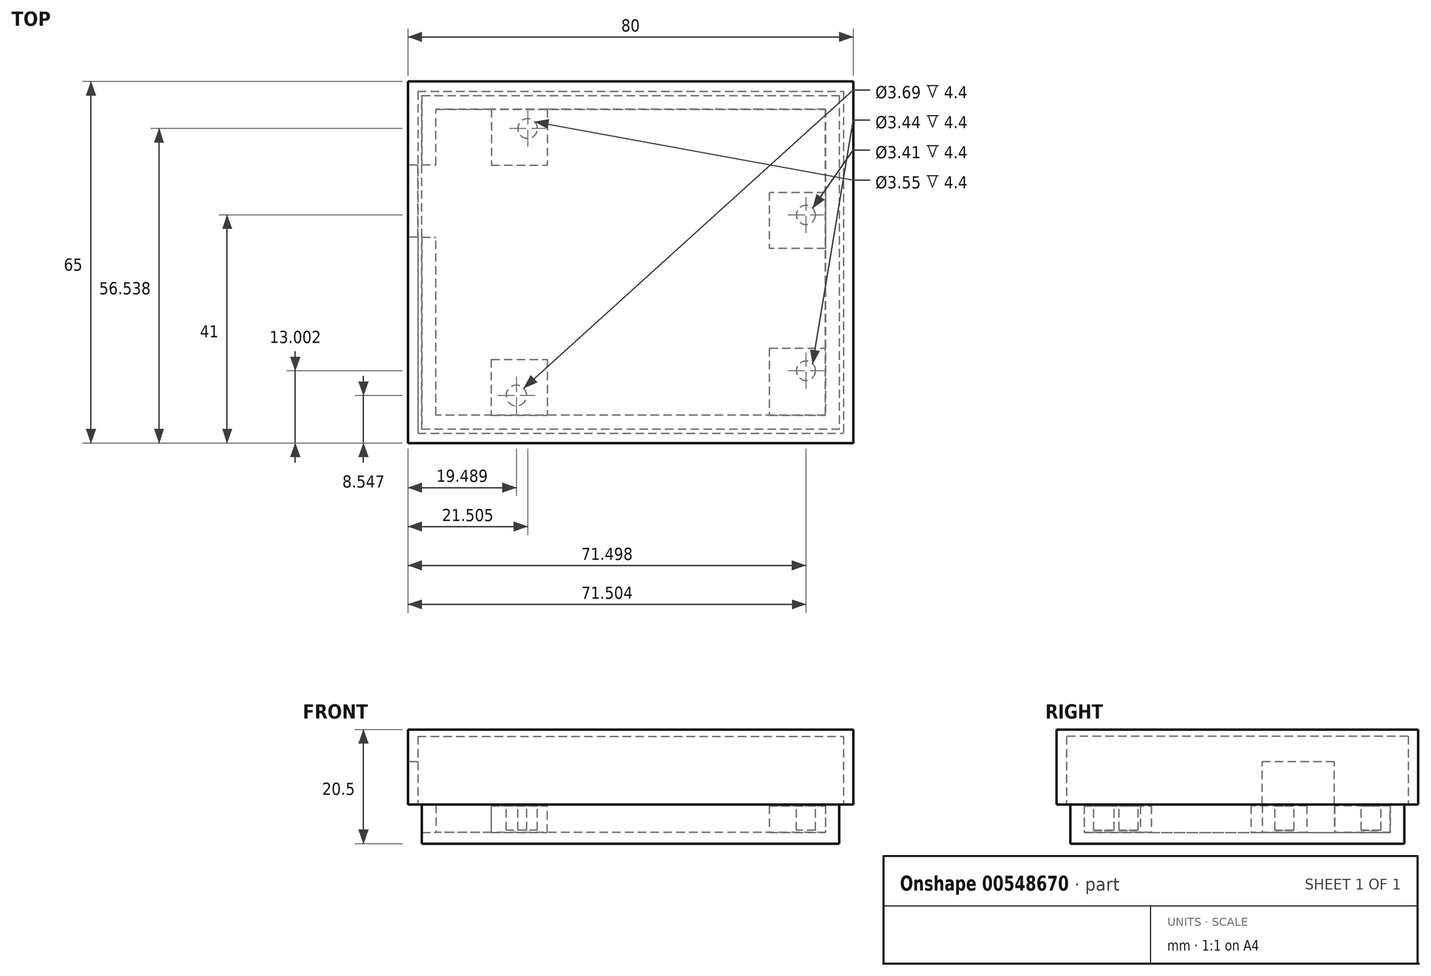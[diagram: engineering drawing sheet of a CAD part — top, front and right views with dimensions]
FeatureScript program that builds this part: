
annotation { "Feature Type Name" : "Feature", "Feature Type Description" : "" }
export const myFeature = defineFeature(function(context is Context, id is Id, definition is map)
    precondition{}
    {
        {
            var Q0;
            Q0=qCreatedBy(makeId("Top.planeOp"),FACE);
            var sketch = newSketch(context, id + "F0", { "sketchPlane" : qUnion([Q0])});
            skLineSegment(sketch, "E0.rect.bottom", {"start": v(37.5, -30) * mm, "end": v(-37.5, -30) * mm});
            skLineSegment(sketch, "E0.rect.top", {"start": v(37.5, 30) * mm, "end": v(-37.5, 30) * mm});
            skLineSegment(sketch, "E0.rect.left", {"start": v(37.5, -30) * mm, "end": v(37.5, 30) * mm});
            skLineSegment(sketch, "E0.rect.right", {"start": v(-37.5, -30) * mm, "end": v(-37.5, 30) * mm});
            skPoint(sketch, "E0.rect.middle", {"position": v(0, 0) * mm});
            skSolve(sketch);
        }
        {
            var Q0;
            Q0=qSketchRegion(id+"F0",true);
            extrude(context, id + "F1", {"entities" : qUnion([Q0]), "depth" : 2 * mm});
        }
        {
            var Q0;
            Q0=makeQuery(id+"F1.opExtrude","CAP_FACE",FACE,{"disambiguationData":[OSD([sQuery(id+"F0.wireOp",EDGE,"E0.rect.bottom"),sQuery(id+"F0.wireOp",EDGE,"E0.rect.top"),sQuery(id+"F0.wireOp",EDGE,"E0.rect.left"),sQuery(id+"F0.wireOp",EDGE,"E0.rect.right")])],"isStart":false});
            var sketch = newSketch(context, id + "F2", { "sketchPlane" : qUnion([Q0])});
            skLineSegment(sketch, "E1.rect.bottom", {"start": v(35, -27.5) * mm, "end": v(-35, -27.5) * mm});
            skLineSegment(sketch, "E1.rect.top", {"start": v(35, 27.5) * mm, "end": v(-35, 27.5) * mm});
            skLineSegment(sketch, "E1.rect.left", {"start": v(35, -27.5) * mm, "end": v(35, 27.5) * mm});
            skLineSegment(sketch, "E1.rect.right", {"start": v(-35, -27.5) * mm, "end": v(-35, 27.5) * mm});
            skPoint(sketch, "E1.rect.middle", {"position": v(0, 0) * mm});
            skLineSegment(sketch, "E2.rect.bottom", {"start": v(37.5, -30) * mm, "end": v(-37.5, -30) * mm});
            skLineSegment(sketch, "E2.rect.top", {"start": v(37.5, 30) * mm, "end": v(-37.5, 30) * mm});
            skLineSegment(sketch, "E2.rect.left", {"start": v(37.5, -30) * mm, "end": v(37.5, 30) * mm});
            skLineSegment(sketch, "E2.rect.right", {"start": v(-37.5, -30) * mm, "end": v(-37.5, 30) * mm});
            skSolve(sketch);
        }
        {
            var Q0;
            Q0=qSketchRegion(id+"F2",true);
            extrude(context, id + "F3", {"entities" : qUnion([Q0]), "operationType" : NewBodyOperationType.ADD, "depth" : 15 * mm});
        }
        {
            var Q0;
            Q0=makeQuery(id+"F1.opExtrude","CAP_FACE",FACE,{"disambiguationData":[OSD([sQuery(id+"F0.wireOp",EDGE,"E0.rect.bottom"),sQuery(id+"F0.wireOp",EDGE,"E0.rect.top"),sQuery(id+"F0.wireOp",EDGE,"E0.rect.left"),sQuery(id+"F0.wireOp",EDGE,"E0.rect.right")])],"isStart":false});
            var sketch = newSketch(context, id + "F4", { "sketchPlane" : qUnion([Q0])});
            skLineSegment(sketch, "E3.bottom", {"start": v(-25, 27.5) * mm, "end": v(-15, 27.5) * mm});
            skLineSegment(sketch, "E3.top", {"start": v(-25, 17.5) * mm, "end": v(-15, 17.5) * mm});
            skLineSegment(sketch, "E3.left", {"start": v(-25, 27.5) * mm, "end": v(-25, 17.5) * mm});
            skLineSegment(sketch, "E3.right", {"start": v(-15, 27.5) * mm, "end": v(-15, 17.5) * mm});
            skLineSegment(sketch, "E4.bottom", {"start": v(-25, -27.5) * mm, "end": v(-15, -27.5) * mm});
            skLineSegment(sketch, "E4.top", {"start": v(-25, -17.5) * mm, "end": v(-15, -17.5) * mm});
            skLineSegment(sketch, "E4.left", {"start": v(-25, -27.5) * mm, "end": v(-25, -17.5) * mm});
            skLineSegment(sketch, "E4.right", {"start": v(-15, -27.5) * mm, "end": v(-15, -17.5) * mm});
            skLineSegment(sketch, "E5.bottom", {"start": v(35, -27.5) * mm, "end": v(25, -27.5) * mm});
            skLineSegment(sketch, "E5.top", {"start": v(35, -15.5) * mm, "end": v(25, -15.5) * mm});
            skLineSegment(sketch, "E5.left", {"start": v(35, -27.5) * mm, "end": v(35, -15.5) * mm});
            skLineSegment(sketch, "E5.right", {"start": v(25, -27.5) * mm, "end": v(25, -15.5) * mm});
            skLineSegment(sketch, "E6.bottom", {"start": v(35, 12.5) * mm, "end": v(25, 12.5) * mm});
            skLineSegment(sketch, "E6.top", {"start": v(35, 2.5) * mm, "end": v(25, 2.5) * mm});
            skLineSegment(sketch, "E6.left", {"start": v(35, 12.5) * mm, "end": v(35, 2.5) * mm});
            skLineSegment(sketch, "E6.right", {"start": v(25, 12.5) * mm, "end": v(25, 2.5) * mm});
            skSolve(sketch);
        }
        {
            var Q0;
            Q0=makeQuery(id+"F4.imprint","IMPRINT",FACE,{"disambiguationData":[TD([[makeQuery(id+"F4.imprint","IMPRINT",EDGE,{"derivedFrom":sQuery(id+"F4.wireOp",EDGE,"E3.top")}),-1.0]])]});
            cPlane(context, id + "F5", {"entities" : qUnion([Q0]), "cplaneType" : CPlaneType.OFFSET, "offset" : 5 * mm, "width" : 150 * mm, "height" : 150 * mm});
        }
        {
            var Q0;
            Q0=makeQuery(id+"F3.opExtrude","SWEPT_FACE",FACE,{"disambiguationData":[OSD([sQuery(id+"F2.wireOp",EDGE,"E1.rect.right")])]});
            var sketch = newSketch(context, id + "F6", { "sketchPlane" : qUnion([Q0])});
            skLineSegment(sketch, "E7.bottom", {"start": v(4.5, 17) * mm, "end": v(17.5, 17) * mm});
            skLineSegment(sketch, "E7.top", {"start": v(4.5, 2) * mm, "end": v(17.5, 2) * mm});
            skLineSegment(sketch, "E7.left", {"start": v(4.5, 17) * mm, "end": v(4.5, 2) * mm});
            skLineSegment(sketch, "E7.right", {"start": v(17.5, 17) * mm, "end": v(17.5, 2) * mm});
            skSolve(sketch);
        }
        {
            var Q0;
            Q0=qSketchRegion(id+"F6",true);
            extrude(context, id + "F7", {"entities" : qUnion([Q0]), "operationType" : NewBodyOperationType.REMOVE, "endBound" : BoundingType.UP_TO_NEXT, "oppositeDirection" : true, "depth" : 25 * mm});
        }
        {
            var Q0;
            Q0=qCreatedBy(id+"F5.planeOp",FACE);
            var sketch = newSketch(context, id + "F8", { "sketchPlane" : qUnion([Q0])});
            skLineSegment(sketch, "E8.bottom", {"start": v(-40, -32.5) * mm, "end": v(40, -32.5) * mm});
            skLineSegment(sketch, "E8.top", {"start": v(-40, 32.5) * mm, "end": v(40, 32.5) * mm});
            skLineSegment(sketch, "E8.left", {"start": v(-40, -32.5) * mm, "end": v(-40, 32.5) * mm});
            skLineSegment(sketch, "E8.right", {"start": v(40, -32.5) * mm, "end": v(40, 32.5) * mm});
            skPoint(sketch, "E8.middle", {"position": v(0, 0) * mm});
            skSolve(sketch);
        }
        {
            var Q0;
            Q0 = qSketchRegion(id + "F8", true);
            extrude(context, id + "F9", {"entities" : qUnion([Q0]), "depth" : 13.5 * mm, "offsetDistance" : 25 * mm});
        }
        {
            var Q0;
            {var subQ27=sQuery(id+"F8.wireOp",EDGE,"E8.top");var subQ36=sQuery(id+"F8.wireOp",EDGE,"E8.bottom");var subQ37=sQuery(id+"F8.wireOp",EDGE,"E8.left");var subQ38=sQuery(id+"F8.wireOp",EDGE,"E8.right");Q0=makeQuery(id+"F9.boolean.opBoolean","SPLIT",FACE,{"disambiguationData":[TD([makeQuery(id+"F1.opExtrude","SWEPT_FACE",FACE,{"disambiguationData":[OSD([sQuery(id+"F0.wireOp",EDGE,"E0.rect.bottom")])]})])],"derivedFrom":makeQuery(id+"F9.opExtrude","CAP_FACE",FACE,{"disambiguationData":[OSD([subQ36,subQ27,subQ37,subQ38])],"isStart":true})});}
            var sketch = newSketch(context, id + "F10", { "sketchPlane" : qUnion([Q0])});
            skLineSegment(sketch, "E9.bottom", {"start": v(-38.22, -30.72) * mm, "end": v(38.22, -30.72) * mm});
            skLineSegment(sketch, "E9.top", {"start": v(-38.22, 30.72) * mm, "end": v(38.22, 30.72) * mm});
            skLineSegment(sketch, "E9.left", {"start": v(-38.22, -30.72) * mm, "end": v(-38.22, 30.72) * mm});
            skLineSegment(sketch, "E9.right", {"start": v(38.22, -30.72) * mm, "end": v(38.22, 30.72) * mm});
            skPoint(sketch, "E9.middle", {"position": v(0, 0) * mm});
            skSolve(sketch);
        }
        {
            var Q0;
            Q0 = qSketchRegion(id + "F10", true);
            extrude(context, id + "F11", {"entities" : qUnion([Q0]), "operationType" : NewBodyOperationType.REMOVE, "oppositeDirection" : true, "depth" : 12.3 * mm, "offsetDistance" : 25 * mm});
        }
        {
            var Q0;
            Q0=makeQuery(id+"F9.opExtrude","SWEPT_FACE",FACE,{"disambiguationData":[OSD([sQuery(id+"F8.wireOp",EDGE,"E8.left")])]});
            var sketch = newSketch(context, id + "F12", { "sketchPlane" : qUnion([Q0])});
            skLineSegment(sketch, "E10.bottom", {"start": v(-17.45, 7) * mm, "end": v(-4.5, 7) * mm});
            skLineSegment(sketch, "E10.top", {"start": v(-17.45, 14.72) * mm, "end": v(-4.5, 14.72) * mm});
            skLineSegment(sketch, "E10.left", {"start": v(-17.45, 7) * mm, "end": v(-17.45, 14.72) * mm});
            skLineSegment(sketch, "E10.right", {"start": v(-4.5, 7) * mm, "end": v(-4.5, 14.72) * mm});
            skSolve(sketch);
        }
        {
            var Q0;
            Q0 = qSketchRegion(id + "F12", true);
            extrude(context, id + "F13", {"entities" : qUnion([Q0]), "operationType" : NewBodyOperationType.REMOVE, "oppositeDirection" : true, "depth" : 25 * mm, "offsetDistance" : 25 * mm});
        }
        {
            var Q0;
            Q0=makeQuery(id+"F4.imprint","IMPRINT",FACE,{"disambiguationData":[TD([[makeQuery(id+"F4.imprint","IMPRINT",EDGE,{"derivedFrom":sQuery(id+"F4.wireOp",EDGE,"E3.top")}),-1.0]])]});
            var sketch = newSketch(context, id + "F14", { "sketchPlane" : qUnion([Q0])});
            skLineSegment(sketch, "E11.bottom", {"start": v(-25.02, 27.52) * mm, "end": v(-14.96, 27.52) * mm});
            skLineSegment(sketch, "E11.top", {"start": v(-25.02, 17.43) * mm, "end": v(-14.96, 17.43) * mm});
            skLineSegment(sketch, "E11.left", {"start": v(-25.02, 27.52) * mm, "end": v(-25.02, 17.43) * mm});
            skLineSegment(sketch, "E11.right", {"start": v(-14.96, 27.52) * mm, "end": v(-14.96, 17.43) * mm});
            skLineSegment(sketch, "E12.bottom", {"start": v(34.99, 12.52) * mm, "end": v(24.9, 12.52) * mm});
            skLineSegment(sketch, "E12.top", {"start": v(34.99, 2.47) * mm, "end": v(24.9, 2.47) * mm});
            skLineSegment(sketch, "E12.left", {"start": v(34.99, 12.52) * mm, "end": v(34.99, 2.47) * mm});
            skLineSegment(sketch, "E12.right", {"start": v(24.9, 12.52) * mm, "end": v(24.9, 2.47) * mm});
            skLineSegment(sketch, "E13.bottom", {"start": v(24.9, -15.45) * mm, "end": v(35.03, -15.45) * mm});
            skLineSegment(sketch, "E13.top", {"start": v(24.9, -27.49) * mm, "end": v(35.03, -27.49) * mm});
            skLineSegment(sketch, "E13.left", {"start": v(24.9, -15.45) * mm, "end": v(24.9, -27.49) * mm});
            skLineSegment(sketch, "E13.right", {"start": v(35.03, -15.45) * mm, "end": v(35.03, -27.49) * mm});
            skLineSegment(sketch, "E14.bottom", {"start": v(-25.04, -17.44) * mm, "end": v(-14.96, -17.44) * mm});
            skLineSegment(sketch, "E14.top", {"start": v(-25.04, -27.49) * mm, "end": v(-14.96, -27.49) * mm});
            skLineSegment(sketch, "E14.left", {"start": v(-25.04, -17.44) * mm, "end": v(-25.04, -27.49) * mm});
            skLineSegment(sketch, "E14.right", {"start": v(-14.96, -17.44) * mm, "end": v(-14.96, -27.49) * mm});
            skSolve(sketch);
        }
        {
            var Q0;
            Q0 = qSketchRegion(id + "F14", true);
            extrude(context, id + "F15", {"entities" : qUnion([Q0]), "operationType" : NewBodyOperationType.ADD, "depth" : 4.8 * mm, "offsetDistance" : 25 * mm});
        }
        {
            var Q0;
            {var subQ6=sQuery(id+"F2.wireOp",EDGE,"E1.rect.top");var subQ9=sQuery(id+"F14.wireOp",EDGE,"E11.left");var subQ10=sQuery(id+"F14.wireOp",EDGE,"E11.top");var subQ11=sQuery(id+"F14.wireOp",EDGE,"E11.right");Q0=makeQuery(id+"F15.boolean.opBoolean","SPLIT",FACE,{"disambiguationData":[TD([makeQuery(id+"F3.opExtrude","SWEPT_FACE",FACE,{"disambiguationData":[OSD([subQ6])]})])],"derivedFrom":makeQuery(id+"F15.opExtrude","CAP_FACE",FACE,{"disambiguationData":[OSD([sQuery(id+"F14.wireOp",EDGE,"E11.bottom"),subQ10,subQ9,subQ11])],"isStart":false})});}
            var sketch = newSketch(context, id + "F16", { "sketchPlane" : qUnion([Q0])});
            skCircle(sketch, "E15", {"center": v(-18.5, 24.04) * mm, "radius": 1.77 * mm});
            skCircle(sketch, "E16", {"center": v(31.5, 8.5) * mm, "radius": 1.7 * mm});
            skCircle(sketch, "E17", {"center": v(31.5, -19.5) * mm, "radius": 1.72 * mm});
            skCircle(sketch, "E18", {"center": v(-20.51, -23.95) * mm, "radius": 1.84 * mm});
            skSolve(sketch);
        }
        {
            var Q0;
            Q0 = qSketchRegion(id + "F16", true);
            extrude(context, id + "F17", {"entities" : qUnion([Q0]), "operationType" : NewBodyOperationType.REMOVE, "oppositeDirection" : true, "depth" : 4.4 * mm, "offsetDistance" : 25 * mm});
        }
    });
